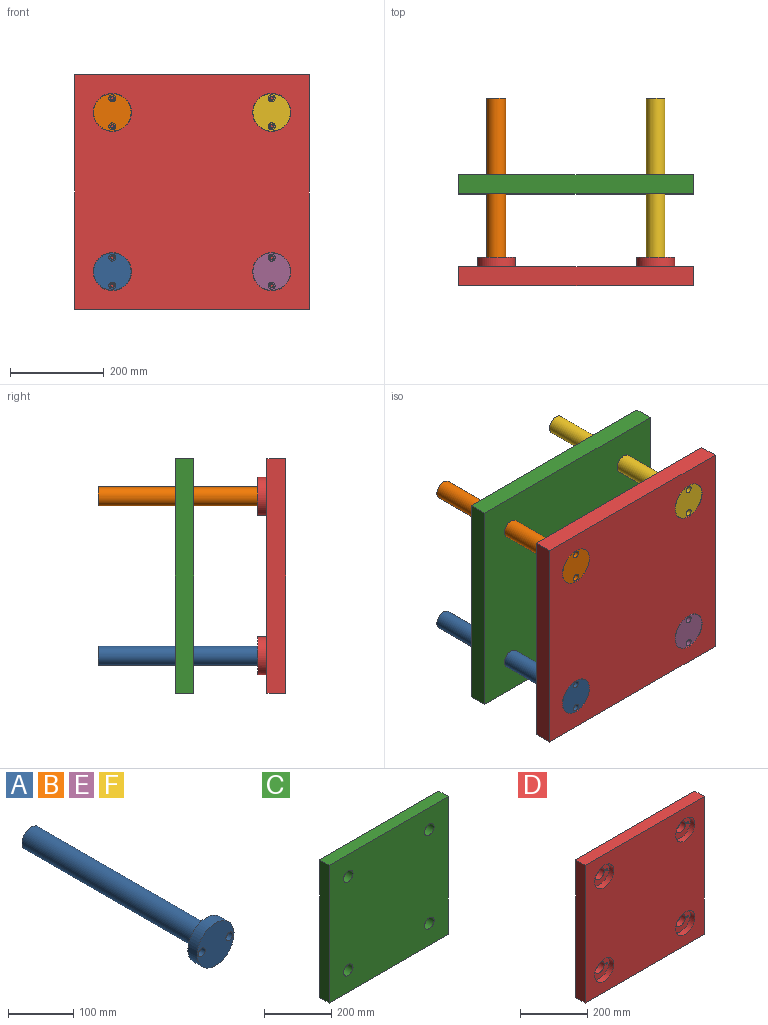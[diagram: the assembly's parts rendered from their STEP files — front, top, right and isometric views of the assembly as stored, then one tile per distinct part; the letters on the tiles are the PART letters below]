
ASSEMBLY  parts=6 mates=12
PART A: 11 faces, bbox 80x400x80 mm
  f0: cylinder r=20mm len=380mm, axis (0,-1,0), area 47752.2mm2, adj f1,f3
  f1: plane 40x40mm, normal (0,1,0), area 1256.6mm2, adj f0
  f2: cylinder r=40mm len=80mm, axis (0,-1,0), area 5026.5mm2, adj f3,f4
  f3: plane 80x80mm, normal (0,1,0), area 3656.4mm2, adj f0,f2,f5,f8
  f4: plane 80x80mm, normal (0,-1,0), area 4673.1mm2, adj f2,f7,f10
  f5: cylinder r=4.25mm len=10mm, axis (0,-1,0), area 267mm2, adj f3,f6
  f6: plane 15x15mm, normal (0,-1,0), area 120mm2, adj f5,f7
  f7: cylinder r=7.5mm len=15mm, axis (0,-1,0), area 471.2mm2, adj f4,f6
  f8: cylinder r=4.25mm len=10mm, axis (0,-1,0), area 267mm2, adj f3,f9
  f9: plane 15x15mm, normal (0,-1,0), area 120mm2, adj f8,f10
  f10: cylinder r=7.5mm len=15mm, axis (0,-1,0), area 471.2mm2, adj f4,f9
PART B: same geometry as A
PART C: 10 faces, bbox 500x40x500 mm
  f0: plane 500x40mm, normal (1,0,0), area 20000mm2, adj f1,f3,f4,f5
  f1: plane 500x40mm, normal (0,0,1), area 20000mm2, adj f0,f2,f4,f5
  f2: plane 500x40mm, normal (-1,0,0), area 20000mm2, adj f1,f3,f4,f5
  f3: plane 500x40mm, normal (0,0,-1), area 20000mm2, adj f0,f2,f4,f5
  f4: plane 500x500mm, normal (0,1,0), area 244973.5mm2, adj f0,f1,f2,f3,f6,f7,f8,f9
  f5: plane 500x500mm, normal (0,-1,0), area 244973.5mm2, adj f0,f1,f2,f3,f6,f7,f8,f9
  f6: cylinder r=20mm len=40mm, axis (0,1,0), area 5026.5mm2, adj f4,f5
  f7: cylinder r=20mm len=40mm, axis (0,1,0), area 5026.5mm2, adj f4,f5
  f8: cylinder r=20mm len=40mm, axis (0,1,0), area 5026.5mm2, adj f4,f5
  f9: cylinder r=20mm len=40mm, axis (0,1,0), area 5026.5mm2, adj f4,f5
PART D: 46 faces, bbox 500x60x500 mm
  f0: plane 500x40mm, normal (1,0,0), area 20000mm2, adj f1,f3,f4,f5
  f1: plane 500x40mm, normal (0,0,1), area 20000mm2, adj f0,f2,f4,f5
  f2: plane 500x40mm, normal (-1,0,0), area 20000mm2, adj f1,f3,f4,f5
  f3: plane 500x40mm, normal (0,0,-1), area 20000mm2, adj f0,f2,f4,f5
  f4: plane 500x500mm, normal (0,1,0), area 229388mm2, adj f0,f1,f2,f3,f27,f34,f39,f44
  f5: plane 500x500mm, normal (0,-1,0), area 229388mm2, adj f0,f1,f2,f3,f8,f11,f14,f17
  f6: cylinder r=20mm len=40mm, axis (0,-1,0), area 2513.3mm2, adj f7,f38
  f7: plane 81x81mm, normal (0,-1,0), area 3823.7mm2, adj f6,f8,f24,f25
  f8: cylinder r=40.5mm len=81mm, axis (0,-1,0), area 5089.4mm2, adj f5,f7
  f9: cylinder r=20mm len=40mm, axis (0,-1,0), area 2513.3mm2, adj f10,f43
  f10: plane 81x81mm, normal (0,-1,0), area 3823.7mm2, adj f9,f11,f22,f23
  f11: cylinder r=40.5mm len=81mm, axis (0,-1,0), area 5089.4mm2, adj f5,f10
  f12: cylinder r=20mm len=40mm, axis (0,-1,0), area 2513.3mm2, adj f13,f33
  f13: plane 81x81mm, normal (0,-1,0), area 3823.7mm2, adj f12,f14,f20,f21
  f14: cylinder r=40.5mm len=81mm, axis (0,-1,0), area 5089.4mm2, adj f5,f13
  f15: cylinder r=20mm len=40mm, axis (0,-1,0), area 2513.3mm2, adj f16,f28
  f16: plane 81x81mm, normal (0,-1,0), area 3823.7mm2, adj f15,f17,f18,f19
  f17: cylinder r=40.5mm len=81mm, axis (0,-1,0), area 5089.4mm2, adj f5,f16
  f18: cylinder r=3.4mm len=20mm, axis (0,-1,0), area 427.3mm2, adj f16,f29
  f19: cylinder r=3.4mm len=20mm, axis (0,-1,0), area 427.3mm2, adj f16,f30
  f20: cylinder r=3.4mm len=20mm, axis (0,-1,0), area 427.3mm2, adj f13,f32
  f21: cylinder r=3.4mm len=20mm, axis (0,-1,0), area 427.3mm2, adj f13,f31
  f22: cylinder r=3.4mm len=20mm, axis (0,-1,0), area 427.3mm2, adj f10,f42
  f23: cylinder r=3.4mm len=20mm, axis (0,-1,0), area 427.3mm2, adj f10,f41
  f24: cylinder r=3.4mm len=20mm, axis (0,-1,0), area 427.3mm2, adj f7,f37
  f25: cylinder r=3.4mm len=20mm, axis (0,-1,0), area 427.3mm2, adj f7,f36
  f26: plane 81x81mm, normal (0,1,0), area 5153mm2, adj f27
  f27: cylinder r=40.5mm len=81mm, axis (0,-1,0), area 5089.4mm2, adj f4,f26
  f28: plane 40x40mm, normal (0,-1,0), area 1256.6mm2, adj f15
  f29: plane 6.8x6.8mm, normal (0,-1,0), area 36.3mm2, adj f18
  f30: plane 6.8x6.8mm, normal (0,-1,0), area 36.3mm2, adj f19
  f31: plane 6.8x6.8mm, normal (0,-1,0), area 36.3mm2, adj f21
  f32: plane 6.8x6.8mm, normal (0,-1,0), area 36.3mm2, adj f20
  f33: plane 40x40mm, normal (0,-1,0), area 1256.6mm2, adj f12
  f34: cylinder r=40.5mm len=81mm, axis (0,-1,0), area 5089.4mm2, adj f4,f35
  f35: plane 81x81mm, normal (0,1,0), area 5153mm2, adj f34
  f36: plane 6.8x6.8mm, normal (0,-1,0), area 36.3mm2, adj f25
  f37: plane 6.8x6.8mm, normal (0,-1,0), area 36.3mm2, adj f24
  f38: plane 40x40mm, normal (0,-1,0), area 1256.6mm2, adj f6
  f39: cylinder r=40.5mm len=81mm, axis (0,-1,0), area 5089.4mm2, adj f4,f40
  f40: plane 81x81mm, normal (0,1,0), area 5153mm2, adj f39
  f41: plane 6.8x6.8mm, normal (0,-1,0), area 36.3mm2, adj f23
  f42: plane 6.8x6.8mm, normal (0,-1,0), area 36.3mm2, adj f22
  f43: plane 40x40mm, normal (0,-1,0), area 1256.6mm2, adj f9
  f44: cylinder r=40.5mm len=81mm, axis (0,-1,0), area 5089.4mm2, adj f4,f45
  f45: plane 81x81mm, normal (0,1,0), area 5153mm2, adj f44
PART E: same geometry as A
PART F: same geometry as A
PLACE A rot(axis=(0,1,0),90deg) t=(864.3,167.42,310.02)mm
PLACE B rot(axis=(0,1,0),90deg) t=(864.3,167.42,650.02)mm
PLACE C rot(axis=(0,1,0),90deg) t=(909.79,213.42,581.55)mm
PLACE D rot(axis=(0,1,0),90deg) t=(909.79,17.42,581.55)mm
PLACE E rot(axis=(0,1,0),90deg) t=(1204.3,167.42,310.02)mm
PLACE F rot(axis=(0,1,0),90deg) t=(1204.3,167.42,650.02)mm
MATE cylindrical E.f5 <-> D.f22  axis (0,-1,0) through (1204.3,27.42,280.02)mm
MATE cylindrical A.f0 <-> D.f12  axis (0,1,0) through (864.3,37.42,310.02)mm
MATE cylindrical F.f0 <-> D.f6  axis (0,1,0) through (1204.3,37.42,650.02)mm
MATE slider C.f8 <-> E.f0  axis (0,-1,0) through (1204.3,213.42,310.02)mm
MATE cylindrical E.f2 <-> D.f9  axis (0,1,0) through (1204.3,37.42,310.02)mm
MATE cylindrical F.f5 <-> D.f25  axis (0,1,0) through (1204.3,37.42,620.02)mm
MATE planar B.f2 <-> D.f15  axis (0,1,0) through (864.3,37.42,650.02)mm
MATE slider B.f2 <-> D.f15  axis (0,1,0) through (864.3,37.42,650.02)mm
MATE cylindrical A.f5 <-> D.f20  axis (0,-1,0) through (864.3,27.42,280.02)mm
MATE cylindrical B.f5 <-> D.f18  axis (0,-1,0) through (864.3,32.42,620.02)mm
MATE planar E.f2 <-> D.f9  axis (0,1,0) through (1204.3,37.42,310.02)mm
MATE planar A.f2 <-> D.f12  axis (0,1,0) through (864.3,37.42,310.02)mm
